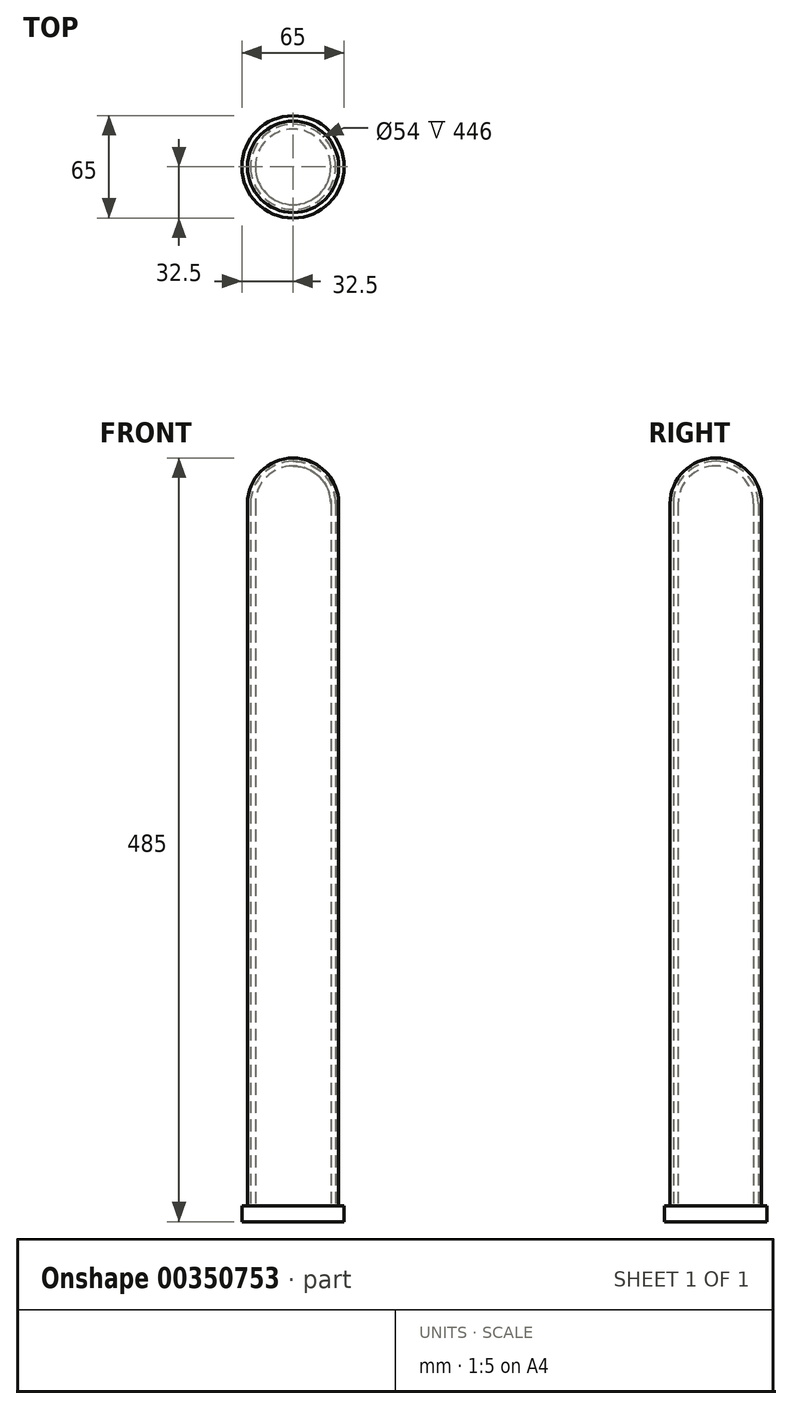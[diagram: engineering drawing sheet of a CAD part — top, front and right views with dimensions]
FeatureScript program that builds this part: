
annotation { "Feature Type Name" : "Feature", "Feature Type Description" : "" }
export const myFeature = defineFeature(function(context is Context, id is Id, definition is map)
    precondition{}
    {
        {
            var Q0;
            Q0=qCreatedBy(makeId("Front.planeOp"),FACE);
            var sketch = newSketch(context, id + "F0", { "sketchPlane" : qUnion([Q0])});
            skLineSegment(sketch, "E0", {"start": v(0, 0) * mm, "end": v(0, 475) * mm});
            skArc(sketch, "E1", {"start": v(29, 446) * mm, "mid": v(20.5, 466.5) * mm, "end": v(0, 475) * mm});
            skLineSegment(sketch, "E2", {"start": v(29, 446) * mm, "end": v(29, 0) * mm});
            skLineSegment(sketch, "E3", {"start": v(29, 0) * mm, "end": v(0, 0) * mm});
            skSolve(sketch);
        }
        {
            var Q0;
            Q0=makeQuery(id+"F0.imprint","IMPRINT",FACE,{"disambiguationData":[TD([[makeQuery(id+"F0.imprint","IMPRINT",EDGE,{"derivedFrom":sQuery(id+"F0.wireOp",EDGE,"E0")}),-1.0]])]});
            var Q1;
            Q1=sQuery(id+"F0.wireOp",EDGE,"E0");
            revolve(context, id + "F1", {"entities" : qUnion([Q0]), "axis" : qUnion([Q1]), "revolveType" : RevolveType.FULL});
        }
        {
            var Q0;
            Q0=makeQuery(id+"F1.opRevolve","SWEPT_FACE",FACE,{"disambiguationData":[OSD([sQuery(id+"F0.wireOp",EDGE,"E3")])]});
            shell(context, id + "F2", {"entities" : qUnion([Q0]), "thickness" : 2 * mm});
        }
        {
            var Q0;
            Q0=qCreatedBy(makeId("Front.planeOp"),FACE);
            var sketch = newSketch(context, id + "F3", { "sketchPlane" : qUnion([Q0])});
            skLineSegment(sketch, "E4", {"start": v(0, 0) * mm, "end": v(0, 470) * mm});
            skArc(sketch, "E5", {"start": v(24, 446) * mm, "mid": v(16.97, 462.97) * mm, "end": v(0, 470) * mm});
            skLineSegment(sketch, "E6", {"start": v(24, 446) * mm, "end": v(24, 0) * mm});
            skLineSegment(sketch, "E7", {"start": v(24, 0) * mm, "end": v(0, 0) * mm});
            skSolve(sketch);
        }
        {
            var Q0;
            Q0 = qSketchRegion(id + "F3", true);
            var Q1;
            Q1=sQuery(id+"F3.wireOp",EDGE,"E4");
            revolve(context, id + "F4", {"entities" : qUnion([Q0]), "axis" : qUnion([Q1]), "revolveType" : RevolveType.FULL});
        }
        {
            var Q0;
            Q0=makeQuery(id+"F4.opRevolve","SWEPT_FACE",FACE,{"disambiguationData":[OSD([sQuery(id+"F3.wireOp",EDGE,"E7")])]});
            var sketch = newSketch(context, id + "F5", { "sketchPlane" : qUnion([Q0])});
            skCircle(sketch, "E8", {"center": v(0, 0) * mm, "radius": 32.5 * mm});
            skSolve(sketch);
        }
        {
            var Q0;
            Q0 = qSketchRegion(id + "F5", true);
            extrude(context, id + "F6", {"entities" : qUnion([Q0]), "depth" : 10 * mm});
        }
    });
